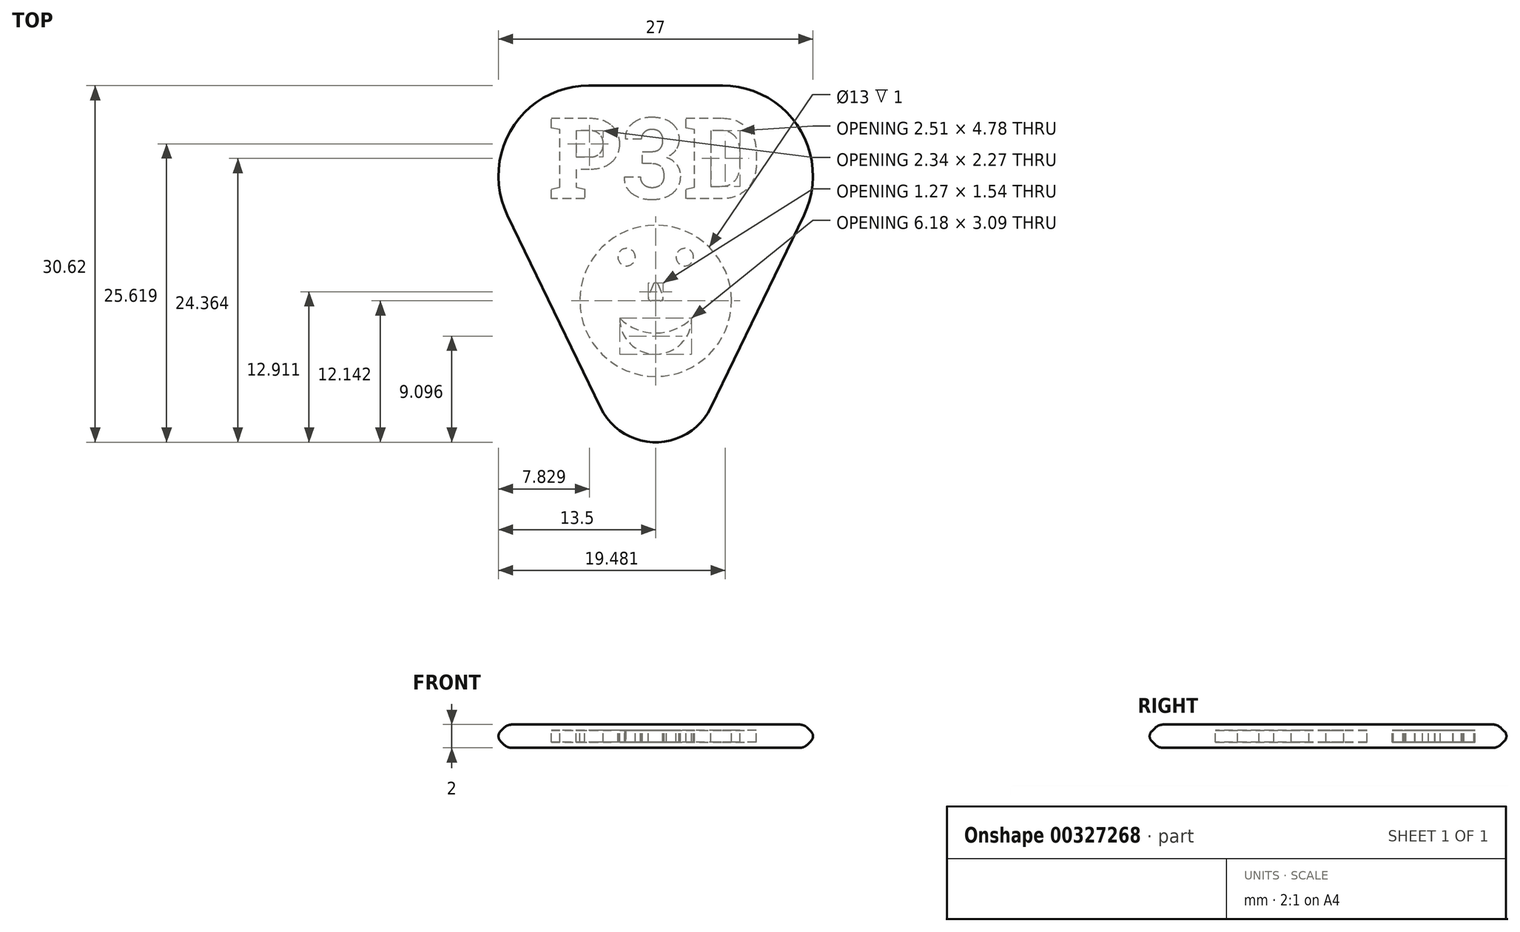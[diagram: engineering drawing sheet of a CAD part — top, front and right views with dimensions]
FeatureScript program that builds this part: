
annotation { "Feature Type Name" : "Feature", "Feature Type Description" : "" }
export const myFeature = defineFeature(function(context is Context, id is Id, definition is map)
    precondition{}
    {
        {
            var Q0;
            Q0=qCreatedBy(makeId("Top.planeOp"),FACE);
            var sketch = newSketch(context, id + "F0", { "sketchPlane" : qUnion([Q0])});
            skLineSegment(sketch, "E0", {"start": v(-5.74, 12.45) * mm, "end": v(5.74, 12.45) * mm});
            skLineSegment(sketch, "E1", {"start": v(12.95, 0.97) * mm, "end": v(4.95, -15.56) * mm});
            skLineSegment(sketch, "E2", {"start": v(-4.95, -15.56) * mm, "end": v(-12.95, 0.97) * mm});
            skPoint(sketch, "E3.visualSharp", {"position": v(-18.5, 12.45) * mm});
            skArc(sketch, "E3.filletArc", {"start": v(-5.74, 12.45) * mm, "mid": v(-12.52, 8.7) * mm, "end": v(-12.95, 0.97) * mm});
            skPoint(sketch, "E4.visualSharp", {"position": v(18.5, 12.45) * mm});
            skArc(sketch, "E4.filletArc", {"start": v(12.95, 0.97) * mm, "mid": v(12.52, 8.7) * mm, "end": v(5.74, 12.45) * mm});
            skPoint(sketch, "E5.visualSharp", {"position": v(0, -25.8) * mm});
            skArc(sketch, "E5.filletArc", {"start": v(-4.95, -15.56) * mm, "mid": v(0, -18.66) * mm, "end": v(4.95, -15.56) * mm});
            skSolve(sketch);
        }
        {
            var Q0;
            Q0=makeQuery(id+"F0.imprint","IMPRINT",FACE,{"disambiguationData":[TD([[makeQuery(id+"F0.imprint","IMPRINT",EDGE,{"derivedFrom":sQuery(id+"F0.wireOp",EDGE,"E0")}),-1.0]])]});
            extrude(context, id + "F1", {"entities" : qUnion([Q0]), "endBound" : BoundingType.SYMMETRIC, "depth" : 2 * mm});
        }
        {
            var Q0;
            Q0=makeQuery(id+"F1.opExtrude","CAP_EDGE",EDGE,{"disambiguationData":[OSD([sQuery(id+"F0.wireOp",EDGE,"E1")])],"isStart":false});
            var Q1;
            Q1=makeQuery(id+"F1.opExtrude","CAP_EDGE",EDGE,{"disambiguationData":[OSD([sQuery(id+"F0.wireOp",EDGE,"E1")])],"isStart":true});
            chamfer(context, id + "F2", {"entities" : qUnion([Q0, Q1]), "chamferType" : ChamferType.OFFSET_ANGLE, "width" : 1 * mm, "oppositeDirection" : false, "angle" : 45 * degree, "tangentPropagation" : true});
        }
        {
            var Q0;
            {var subQ0=sQuery(id+"F0.wireOp",EDGE,"E2");Q0=makeQuery(id+"F2.opChamfer","BLEND_EDGE",EDGE,{"blendedFrom":[makeQuery(id+"F1.opExtrude","CAP_EDGE",EDGE,{"disambiguationData":[OSD([subQ0])],"isStart":false}),makeQuery(id+"F1.opExtrude","CAP_FACE",FACE,{"disambiguationData":[OSD([sQuery(id+"F0.wireOp",EDGE,"E0"),sQuery(id+"F0.wireOp",EDGE,"E1"),subQ0,sQuery(id+"F0.wireOp",EDGE,"E3.filletArc"),sQuery(id+"F0.wireOp",EDGE,"E4.filletArc"),sQuery(id+"F0.wireOp",EDGE,"E5.filletArc")])],"isStart":false})],"blendedInto":[makeQuery(id+"F1.opExtrude","CAP_FACE",FACE,{"disambiguationData":[OSD([sQuery(id+"F0.wireOp",EDGE,"E0"),sQuery(id+"F0.wireOp",EDGE,"E1"),subQ0,sQuery(id+"F0.wireOp",EDGE,"E3.filletArc"),sQuery(id+"F0.wireOp",EDGE,"E4.filletArc"),sQuery(id+"F0.wireOp",EDGE,"E5.filletArc")])],"isStart":false})]});}
            var Q1;
            {var subQ0=sQuery(id+"F0.wireOp",EDGE,"E1");Q1=makeQuery(id+"F2.opChamfer","BLEND_EDGE",EDGE,{"blendedFrom":[makeQuery(id+"F1.opExtrude","CAP_EDGE",EDGE,{"disambiguationData":[OSD([subQ0])],"isStart":true}),makeQuery(id+"F1.opExtrude","CAP_FACE",FACE,{"disambiguationData":[OSD([sQuery(id+"F0.wireOp",EDGE,"E0"),subQ0,sQuery(id+"F0.wireOp",EDGE,"E2"),sQuery(id+"F0.wireOp",EDGE,"E3.filletArc"),sQuery(id+"F0.wireOp",EDGE,"E4.filletArc"),sQuery(id+"F0.wireOp",EDGE,"E5.filletArc")])],"isStart":true})],"blendedInto":[makeQuery(id+"F1.opExtrude","CAP_FACE",FACE,{"disambiguationData":[OSD([sQuery(id+"F0.wireOp",EDGE,"E0"),subQ0,sQuery(id+"F0.wireOp",EDGE,"E2"),sQuery(id+"F0.wireOp",EDGE,"E3.filletArc"),sQuery(id+"F0.wireOp",EDGE,"E4.filletArc"),sQuery(id+"F0.wireOp",EDGE,"E5.filletArc")])],"isStart":true})]});}
            fillet(context, id + "F3", {"entities" : qUnion([Q0, Q1]), "radius" : 1 * mm, "tangentPropagation" : true, "allowEdgeOverflow" : false});
        }
        {
            var Q0;
            Q0=qCreatedBy(makeId("Top.planeOp"),FACE);
            var sketch = newSketch(context, id + "F4", { "sketchPlane" : qUnion([Q0])});
            skText(sketch, "E6", { "text": "P3D", "fontName": "RobotoSlab-Bold.ttf"});
            const initialGuessF4  = {"E6": [-0.00923, 0.0025, 1, 0, 0.007]};
            skSetInitialGuess(sketch, initialGuessF4);
            skSolve(sketch);
        }
        {
            var Q0;
            Q0=qSketchRegion(id+"F4",true);
            extrude(context, id + "F5", {"entities" : qUnion([Q0]), "operationType" : NewBodyOperationType.REMOVE, "endBound" : BoundingType.SYMMETRIC, "oppositeDirection" : true, "depth" : 1 * mm, "offsetDistance" : 25 * mm});
        }
        {
            var Q0;
            {var subQ0=sQuery(id+"F0.wireOp",EDGE,"E2");Q0=makeQuery(id+"F2.opChamfer","BLEND_EDGE",EDGE,{"blendedFrom":[makeQuery(id+"F1.opExtrude","CAP_EDGE",EDGE,{"disambiguationData":[OSD([subQ0])],"isStart":true}),makeQuery(id+"F1.opExtrude","CAP_EDGE",EDGE,{"disambiguationData":[OSD([subQ0])],"isStart":false})],"blendedInto":[]});}
            fillet(context, id + "F6", {"entities" : qUnion([Q0]), "radius" : 0.6 * mm, "tangentPropagation" : true, "allowEdgeOverflow" : false});
        }
        {
            var Q0;
            Q0=qCreatedBy(makeId("Top.planeOp"),FACE);
            var sketch = newSketch(context, id + "F7", { "sketchPlane" : qUnion([Q0])});
            skCircle(sketch, "E7", {"center": v(0, -6.27) * mm, "radius": 6.5 * mm});
            skCircle(sketch, "E8", {"center": v(-2.5, -2.52) * mm, "radius": 0.75 * mm});
            skCircle(sketch, "E9.MirrorC", {"center": v(2.5, -2.52) * mm, "radius": 0.75 * mm});
            skArc(sketch, "E10", {"start": v(-3.1, -7.77) * mm, "mid": v(0, -10.86) * mm, "end": v(3.1, -7.77) * mm});
            skLineSegment(sketch, "E11", {"start": v(-0.23, -4.9) * mm, "end": v(-0.62, -5.93) * mm});
            skLineSegment(sketch, "E12", {"start": v(-0.39, -6.27) * mm, "end": v(0, -6.27) * mm});
            skLineSegment(sketch, "E13.MirrorCS", {"start": v(0.23, -4.9) * mm, "end": v(0.62, -5.93) * mm});
            skLineSegment(sketch, "E14.MirrorCS", {"start": v(0.39, -6.27) * mm, "end": v(0, -6.27) * mm});
            skPoint(sketch, "E15.visualSharp", {"position": v(0, -4.27) * mm});
            skArc(sketch, "E15.filletArc", {"start": v(0.23, -4.9) * mm, "mid": v(0, -4.73) * mm, "end": v(-0.23, -4.9) * mm});
            skPoint(sketch, "E16.visualSharp", {"position": v(-0.75, -6.27) * mm});
            skArc(sketch, "E16.filletArc", {"start": v(-0.62, -5.93) * mm, "mid": v(-0.6, -6.16) * mm, "end": v(-0.39, -6.27) * mm});
            skPoint(sketch, "E17.visualSharp", {"position": v(0.75, -6.27) * mm});
            skArc(sketch, "E17.filletArc", {"start": v(0.39, -6.27) * mm, "mid": v(0.6, -6.16) * mm, "end": v(0.62, -5.93) * mm});
            skArc(sketch, "E18", {"start": v(-3.1, -7.77) * mm, "mid": v(0, -9.04) * mm, "end": v(3.1, -7.77) * mm});
            skSolve(sketch);
        }
        {
            var Q0;
            Q0=qSketchRegion(id+"F7",true);
            var Q1;
            Q1=makeQuery(id+"F7.imprint","IMPRINT",FACE,{"disambiguationData":[TD([[makeQuery(id+"F7.imprint","IMPRINT",EDGE,{"derivedFrom":sQuery(id+"F7.wireOp",EDGE,"b4bf5cf7-47f6-4e07-859f-e1e6065c9dbf.0")}),-1.0]])]});
            var Q2;
            Q2=makeQuery(id+"F7.imprint","IMPRINT",FACE,{"disambiguationData":[TD([[makeQuery(id+"F7.imprint","IMPRINT",EDGE,{"derivedFrom":sQuery(id+"F7.wireOp",EDGE,"6f85d2ec-8929-457e-84c4-58013a10ac05.0")}),-1.0]])]});
            extrude(context, id + "F8", {"entities" : qUnion([Q0, Q1, Q2]), "operationType" : NewBodyOperationType.REMOVE, "endBound" : BoundingType.SYMMETRIC, "oppositeDirection" : true, "depth" : 1 * mm, "offsetDistance" : 25 * mm});
        }
    });
